# Revit family: Fan_Coil-Riser_Heat_Exchanger-Whalen-Vertical_Stacked-50_50
name_source: partatom
category: Mechanical Equipment
revit_build: Autodesk Revit MEP 2012 (Build: 20110916_2132(x64)
units: mm (PartAtom-declared; Revit-internal decimal feet)

## types (11) — shared parameters
Date Last Modified = 1/8/2013
Equipment Abbreviation = 5050
Family Version = 1.1.0
Frequency = 60 Hz
Load Classification = HVAC
Manufacturer = The Whalen Company
Model Disclaimer = Contact The Whalen Company for More Information
Power Factor = 0.8
Product Documentation Link = http://www.whalencompany.com
Product Material = Steel - Whalen - Galvanized
Provide Feedback = https://www.surveymonkey.com
URL = http://www.whalencompany.com

## per-type parameters (varying)
| type | Actual Return Air Flow | Actual Supply Air Flow | Description | Model | Weight | zz Integer 1 |
| 0,300 CFM | 200 CFM | 200 CFM | 50/50 Riser Heat-Exchanger Vertical Fan-Coil Units, 300 CFM | W3022 | 215.00 lb | 300 |
| 0,400 CFM | 444 CFM | 444 CFM | 50/50 Riser Heat-Exchanger Vertical Fan-Coil Units, 400 CFM | W4022 | 215.00 lb | 400 |
| 0,500 CFM | 500 CFM | 500 CFM | 50/50 Riser Heat-Exchanger Vertical Fan-Coil Units, 500 CFM | W5022 | 215.00 lb | 500 |
| 0,600 CFM | 482 CFM | 482 CFM | 50/50 Riser Heat-Exchanger Vertical Fan-Coil Units, 600 CFM | W6022 | 215.00 lb | 600 |
| 0,800 CFM | 724 CFM | 724 CFM | 50/50 Riser Heat-Exchanger Vertical Fan-Coil Units, 800 CFM | W8022 | 280.00 lb | 800 |
| 1,000 CFM | 910 CFM | 910 CFM | 50/50 Riser Heat-Exchanger Vertical Fan-Coil Units, 1000 CFM | W10022 | 280.00 lb | 1000 |
| 1,200 CFM | 1160 CFM | 1160 CFM | 50/50 Riser Heat-Exchanger Vertical Fan-Coil Units, 1200 CFM | W12022 | 310.00 lb | 1200 |
| 1,600 CFM | 1600 CFM | 1600 CFM | 50/50 Riser Heat-Exchanger Vertical Fan-Coil Units, 1600 CFM | W16022 | 310.00 lb | 1600 |
| 0,400 CFM, Extended | 444 CFM | 444 CFM | 50/50 Riser Heat-Exchanger Vertical Fan-Coil Units, 400 CFM | W4022X | 0.00 lb | 401 |
| 0,500 CFM, Extended | 500 CFM | 500 CFM | 50/50 Riser Heat-Exchanger Vertical Fan-Coil Units, 500 CFM | W5022X | 0.00 lb | 501 |
| 0,600 CFM, Extended | 482 CFM | 482 CFM | 50/50 Riser Heat-Exchanger Vertical Fan-Coil Units, 600 CFM | W6022X | 215.00 lb | 601 |

## geometry (parser evidence)
native form markers: Blend x8, Sweep x4
no freeform markers — native parametric forms only
